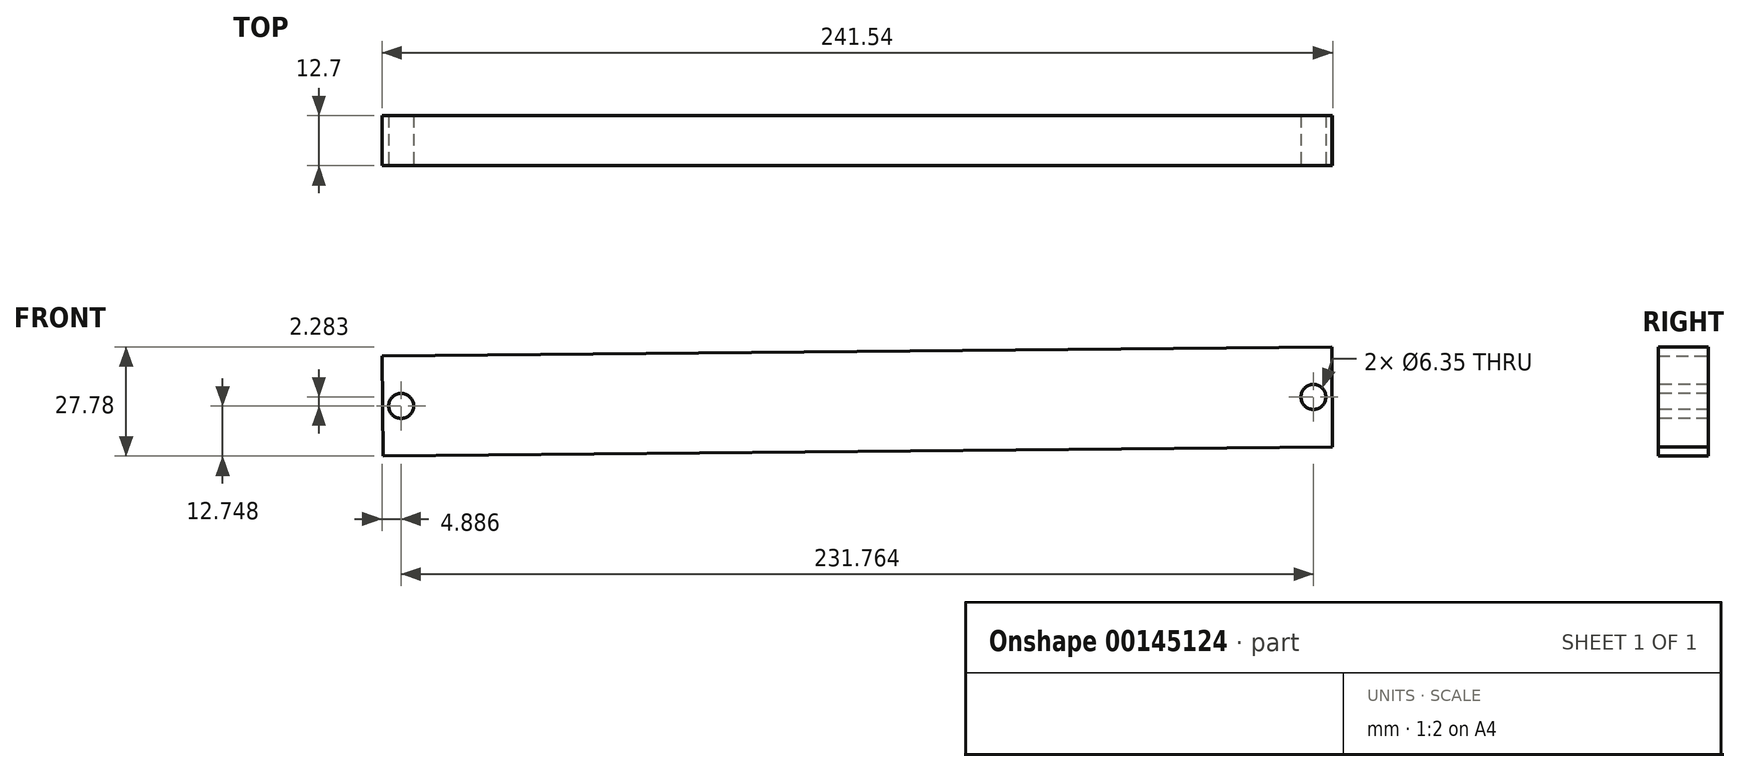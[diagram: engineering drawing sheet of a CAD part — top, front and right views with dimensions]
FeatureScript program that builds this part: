
annotation { "Feature Type Name" : "Feature", "Feature Type Description" : "" }
export const myFeature = defineFeature(function(context is Context, id is Id, definition is map)
    precondition{}
    {
        {
            var Q0;
            Q0=qCreatedBy(makeId("Front.planeOp"),FACE);
            var sketch = newSketch(context, id + "F0", { "sketchPlane" : qUnion([Q0])});
            skLineSegment(sketch, "E0", {"start": v(-83.32, 12.07) * mm, "end": v(157.97, 14.45) * mm});
            skLineSegment(sketch, "E1", {"start": v(-83.32, 12.07) * mm, "end": v(-83.07, -13.33) * mm});
            skLineSegment(sketch, "E2", {"start": v(-83.07, -13.33) * mm, "end": v(158.22, -10.95) * mm});
            skLineSegment(sketch, "E3", {"start": v(158.22, -10.95) * mm, "end": v(157.97, 14.45) * mm});
            skSolve(sketch);
        }
        {
            var Q0;
            Q0 = qSketchRegion(id + "F0", true);
            extrude(context, id + "F1", {"entities" : qUnion([Q0]), "depth" : 12.7 * mm});
        }
        {
            var Q0;
            Q0=makeQuery(id+"F1.opExtrude","CAP_FACE",FACE,{"disambiguationData":[OSD([sQuery(id+"F0.wireOp",EDGE,"E0"),sQuery(id+"F0.wireOp",EDGE,"E1"),sQuery(id+"F0.wireOp",EDGE,"E2"),sQuery(id+"F0.wireOp",EDGE,"E3")])],"isStart":false});
            var sketch = newSketch(context, id + "F2", { "sketchPlane" : qUnion([Q0])});
            skLineSegment(sketch, "E4", {"start": v(-83.32, 12.07) * mm, "end": v(-83.2, -0.63) * mm});
            skLineSegment(sketch, "E5", {"start": v(-83.2, -0.63) * mm, "end": v(-78.43, -0.58) * mm});
            skCircle(sketch, "E6", {"center": v(-78.43, -0.58) * mm, "radius": 3.18 * mm});
            skLineSegment(sketch, "E7", {"start": v(157.97, 14.45) * mm, "end": v(158.1, 1.75) * mm});
            skLineSegment(sketch, "E8", {"start": v(158.1, 1.75) * mm, "end": v(153.33, 1.7) * mm});
            skCircle(sketch, "E9", {"center": v(153.33, 1.7) * mm, "radius": 3.18 * mm});
            skSolve(sketch);
        }
        {
            var Q0;
            Q0 = qSketchRegion(id + "F2", true);
            extrude(context, id + "F3", {"entities" : qUnion([Q0]), "operationType" : NewBodyOperationType.REMOVE, "endBound" : BoundingType.THROUGH_ALL, "oppositeDirection" : true, "depth" : 25.4 * mm});
        }
    });
